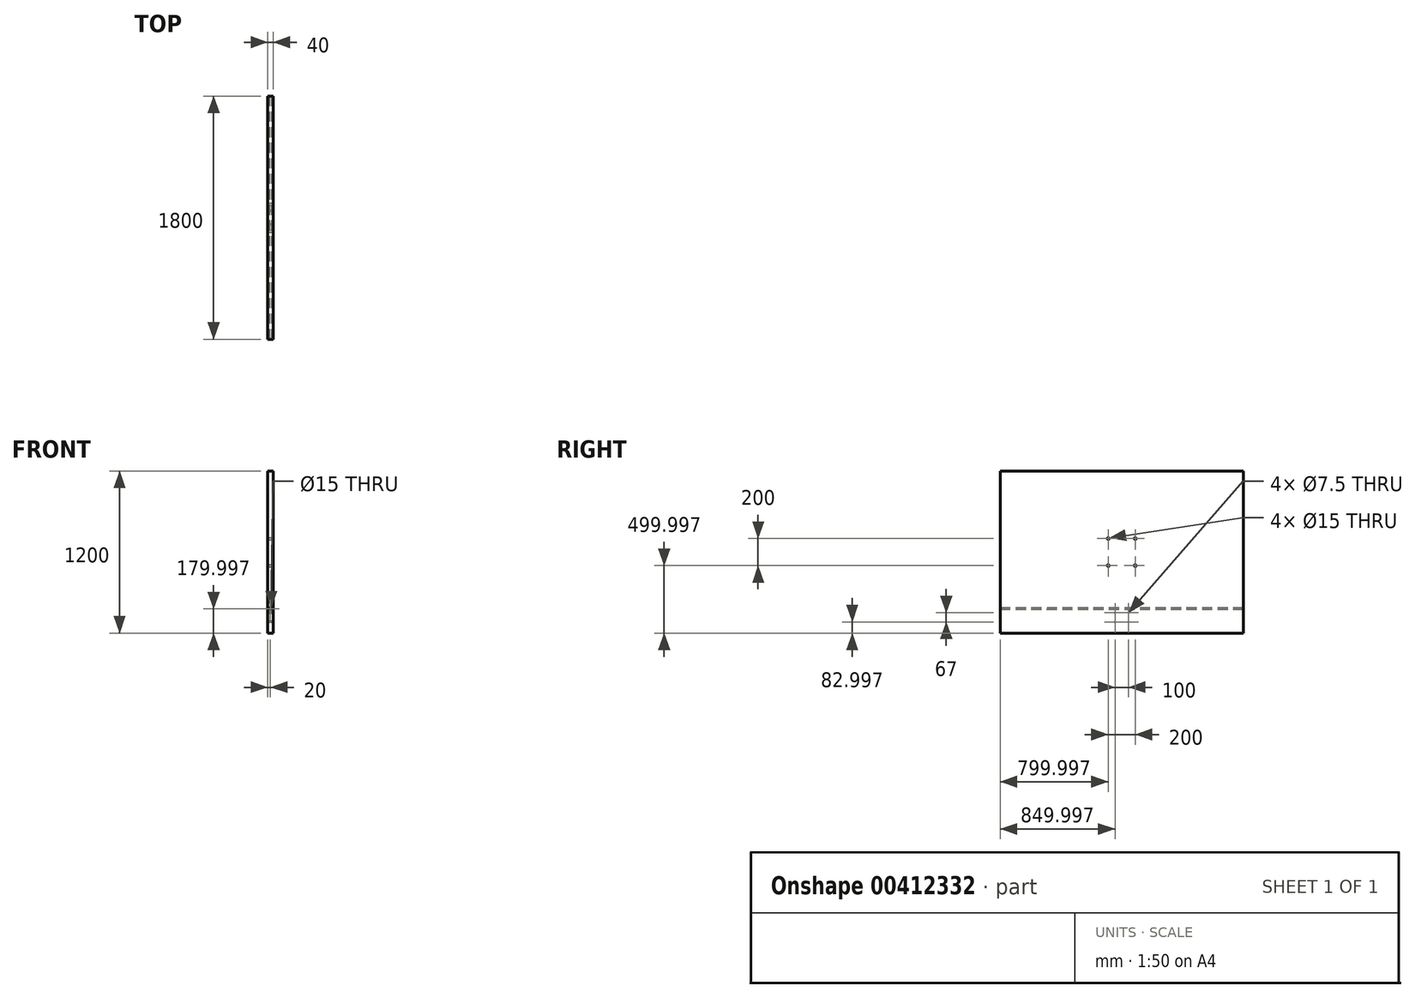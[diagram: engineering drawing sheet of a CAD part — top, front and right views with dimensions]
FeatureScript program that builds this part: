
annotation { "Feature Type Name" : "Feature", "Feature Type Description" : "" }
export const myFeature = defineFeature(function(context is Context, id is Id, definition is map)
    precondition{}
    {
        {
            var Q0;
            Q0=qCreatedBy(makeId("Right.planeOp"),FACE);
            var sketch = newSketch(context, id + "F0", { "sketchPlane" : qUnion([Q0])});
            skLineSegment(sketch, "E0.bottom", {"start": v(-59.1, 1161.05) * mm, "end": v(1740.9, 1161.05) * mm});
            skLineSegment(sketch, "E0.top", {"start": v(-59.1, -38.95) * mm, "end": v(1740.9, -38.95) * mm});
            skLineSegment(sketch, "E0.left", {"start": v(-59.1, 1161.05) * mm, "end": v(-59.1, -38.95) * mm});
            skLineSegment(sketch, "E0.right", {"start": v(1740.9, 1161.05) * mm, "end": v(1740.9, -38.95) * mm});
            skSolve(sketch);
        }
        {
            var Q0;
            Q0 = qSketchRegion(id + "F0", true);
            extrude(context, id + "F1", {"entities" : qUnion([Q0]), "depth" : 40 * mm});
        }
        {
            var Q0;
            Q0=makeQuery(id+"F1.opExtrude","SWEPT_FACE",FACE,{"disambiguationData":[OSD([sQuery(id+"F0.wireOp",EDGE,"E0.left")])]});
            var sketch = newSketch(context, id + "F2", { "sketchPlane" : qUnion([Q0])});
            skLineSegment(sketch, "E1", {"start": v(20, -38.95) * mm, "end": v(20, 141.05) * mm, "construction": true});
            skPoint(sketch, "E2", {"position": v(20, 141.05) * mm});
            skSolve(sketch);
        }
        {
            var Q0;
            Q0=sQuery(id+"F2.wireOp",VERTEX,"E2");
            var Q1;
            Q1=makeQuery(id+"F1.opExtrude","SWEPT_BODY",BODY,{"disambiguationData":[OSD([sQuery(id+"F0.wireOp",EDGE,"E0.bottom"),sQuery(id+"F0.wireOp",EDGE,"E0.top"),sQuery(id+"F0.wireOp",EDGE,"E0.left"),sQuery(id+"F0.wireOp",EDGE,"E0.right")])]});
            hole(context, id + "F3", {"style" : HoleStyle.SIMPLE, "endStyle" : HoleEndStyle.THROUGH, "holeDiameter" : 15 * mm, "isTappedThrough" : true, "tappedDepth" : 12 * mm, "tapClearance" : 3, "startFromSketch" : true, "locations" : qUnion([Q0]), "scope" : qUnion([Q1])});
        }
        {
            var Q0;
            Q0=makeQuery(id+"F1.opExtrude","CAP_FACE",FACE,{"disambiguationData":[OSD([sQuery(id+"F0.wireOp",EDGE,"E0.bottom"),sQuery(id+"F0.wireOp",EDGE,"E0.top"),sQuery(id+"F0.wireOp",EDGE,"E0.left"),sQuery(id+"F0.wireOp",EDGE,"E0.right")])],"isStart":true});
            var sketch = newSketch(context, id + "F4", { "sketchPlane" : qUnion([Q0])});
            skLineSegment(sketch, "E3.bottom", {"start": v(-890.9, 111.05) * mm, "end": v(-790.9, 111.05) * mm, "construction": true});
            skLineSegment(sketch, "E3.top", {"start": v(-890.9, 44.05) * mm, "end": v(-790.9, 44.05) * mm, "construction": true});
            skLineSegment(sketch, "E3.left", {"start": v(-890.9, 111.05) * mm, "end": v(-890.9, 44.05) * mm, "construction": true});
            skLineSegment(sketch, "E3.right", {"start": v(-790.9, 111.05) * mm, "end": v(-790.9, 44.05) * mm, "construction": true});
            skLineSegment(sketch, "E4", {"start": v(-840.9, 1161.05) * mm, "end": v(-840.9, -38.95) * mm, "construction": true});
            skSolve(sketch);
        }
        {
            var Q0;
            Q0=sQuery(id+"F4.wireOp",VERTEX,"E3.bottom.start");
            var Q1;
            Q1=sQuery(id+"F4.wireOp",VERTEX,"E3.left.end");
            var Q2;
            Q2=sQuery(id+"F4.wireOp",VERTEX,"E3.right.end");
            var Q3;
            Q3=sQuery(id+"F4.wireOp",VERTEX,"E3.bottom.end");
            var Q4;
            Q4=makeQuery(id+"F1.opExtrude","SWEPT_BODY",BODY,{"disambiguationData":[OSD([sQuery(id+"F0.wireOp",EDGE,"E0.bottom"),sQuery(id+"F0.wireOp",EDGE,"E0.top"),sQuery(id+"F0.wireOp",EDGE,"E0.left"),sQuery(id+"F0.wireOp",EDGE,"E0.right")])]});
            hole(context, id + "F5", {"style" : HoleStyle.SIMPLE, "endStyle" : HoleEndStyle.BLIND, "holeDiameter" : 7.5 * mm, "holeDepth" : 35 * mm, "isTappedThrough" : true, "tappedDepth" : 12 * mm, "tapClearance" : 3, "startFromSketch" : true, "locations" : qUnion([Q0, Q1, Q2, Q3]), "scope" : qUnion([Q4])});
        }
        {
            var Q0;
            Q0=makeQuery(id+"F1.opExtrude","CAP_FACE",FACE,{"disambiguationData":[OSD([sQuery(id+"F0.wireOp",EDGE,"E0.bottom"),sQuery(id+"F0.wireOp",EDGE,"E0.top"),sQuery(id+"F0.wireOp",EDGE,"E0.left"),sQuery(id+"F0.wireOp",EDGE,"E0.right")])],"isStart":false});
            var sketch = newSketch(context, id + "F6", { "sketchPlane" : qUnion([Q0])});
            skLineSegment(sketch, "E5", {"start": v(840.9, 1161.05) * mm, "end": v(840.9, -38.95) * mm, "construction": true});
            skLineSegment(sketch, "E6", {"start": v(-59.1, 561.05) * mm, "end": v(1740.9, 561.05) * mm, "construction": true});
            skLineSegment(sketch, "E7.bottom", {"start": v(740.9, 661.05) * mm, "end": v(940.9, 661.05) * mm, "construction": true});
            skLineSegment(sketch, "E7.top", {"start": v(740.9, 461.05) * mm, "end": v(940.9, 461.05) * mm, "construction": true});
            skLineSegment(sketch, "E7.left", {"start": v(740.9, 661.05) * mm, "end": v(740.9, 461.05) * mm, "construction": true});
            skLineSegment(sketch, "E7.right", {"start": v(940.9, 661.05) * mm, "end": v(940.9, 461.05) * mm, "construction": true});
            skLineSegment(sketch, "E8", {"start": v(840.9, 461.05) * mm, "end": v(840.9, 661.05) * mm, "construction": true});
            skLineSegment(sketch, "E9", {"start": v(740.9, 561.05) * mm, "end": v(940.9, 561.05) * mm, "construction": true});
            skPoint(sketch, "E10", {"position": v(840.9, 561.05) * mm});
            skSolve(sketch);
        }
        {
            var Q0;
            Q0=sQuery(id+"F6.wireOp",VERTEX,"E7.bottom.start");
            var Q1;
            Q1=sQuery(id+"F6.wireOp",VERTEX,"E7.bottom.end");
            var Q2;
            Q2=sQuery(id+"F6.wireOp",VERTEX,"E7.right.end");
            var Q3;
            Q3=sQuery(id+"F6.wireOp",VERTEX,"E7.top.start");
            var Q4;
            Q4=makeQuery(id+"F1.opExtrude","SWEPT_BODY",BODY,{"disambiguationData":[OSD([sQuery(id+"F0.wireOp",EDGE,"E0.bottom"),sQuery(id+"F0.wireOp",EDGE,"E0.top"),sQuery(id+"F0.wireOp",EDGE,"E0.left"),sQuery(id+"F0.wireOp",EDGE,"E0.right")])]});
            hole(context, id + "F7", {"style" : HoleStyle.SIMPLE, "endStyle" : HoleEndStyle.BLIND, "holeDiameter" : 15 * mm, "holeDepth" : 35 * mm, "isTappedThrough" : true, "tappedDepth" : 12 * mm, "tapClearance" : 3, "startFromSketch" : true, "locations" : qUnion([Q0, Q1, Q2, Q3]), "scope" : qUnion([Q4])});
        }
    });
